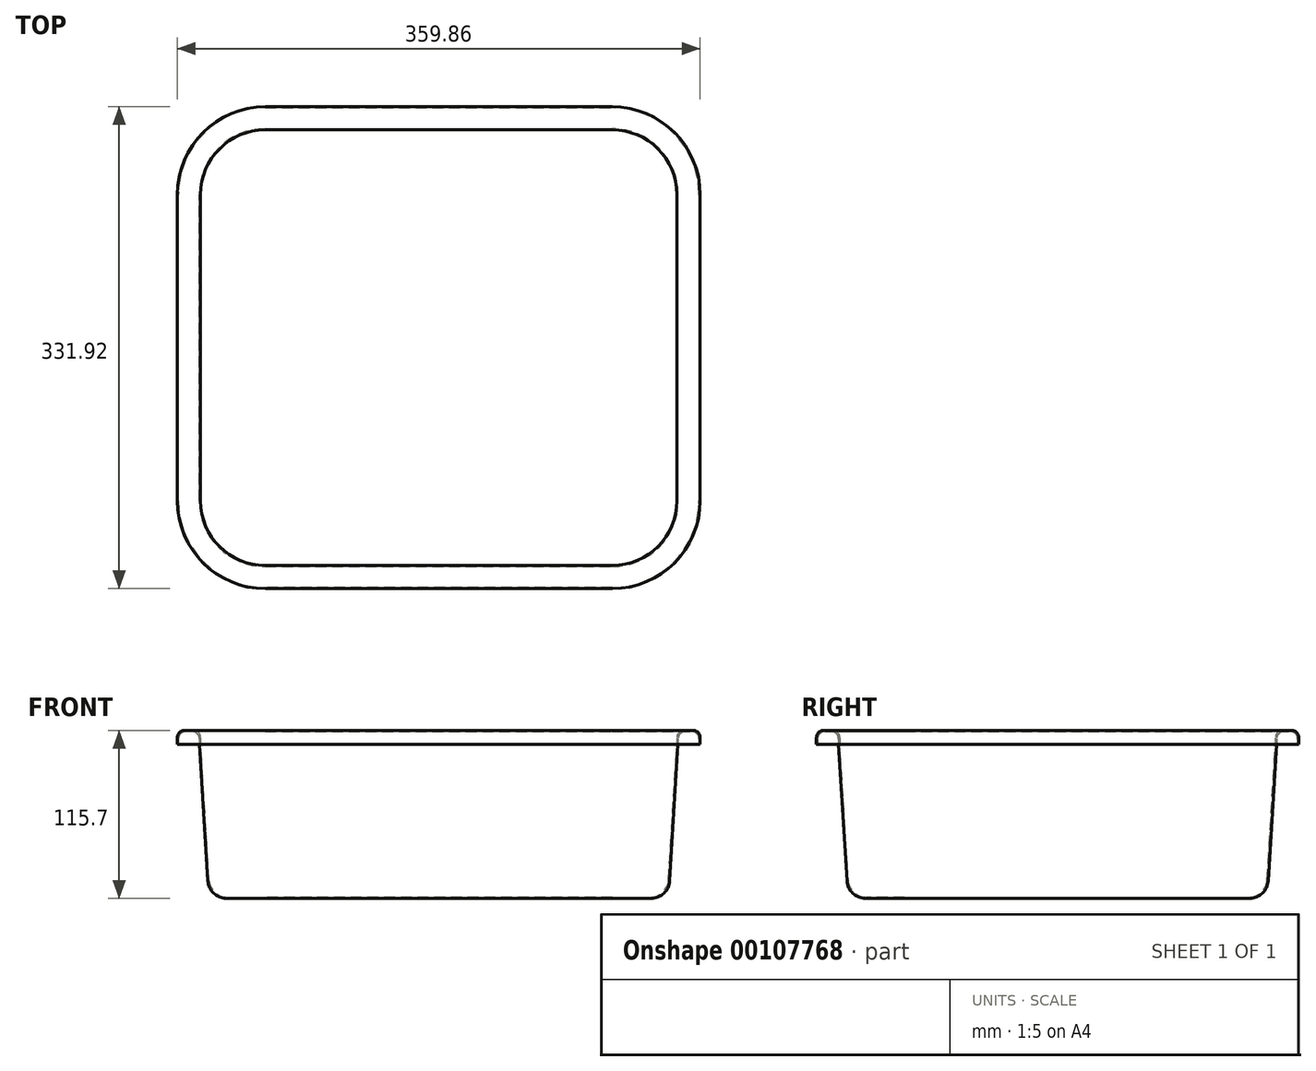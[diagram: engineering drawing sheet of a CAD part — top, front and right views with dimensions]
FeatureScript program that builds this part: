
annotation { "Feature Type Name" : "Feature", "Feature Type Description" : "" }
export const myFeature = defineFeature(function(context is Context, id is Id, definition is map)
    precondition{}
    {
        {
            var Q0;
            Q0=qCreatedBy(makeId("Top.planeOp"),FACE);
            var sketch = newSketch(context, id + "F0", { "sketchPlane" : qUnion([Q0])});
            skLineSegment(sketch, "E0.bottom", {"start": v(-119.38, -143.51) * mm, "end": v(119.38, -143.51) * mm});
            skLineSegment(sketch, "E0.top", {"start": v(-119.38, 143.51) * mm, "end": v(119.38, 143.51) * mm});
            skLineSegment(sketch, "E0.left", {"start": v(-157.48, -105.41) * mm, "end": v(-157.48, 105.41) * mm});
            skLineSegment(sketch, "E0.right", {"start": v(157.48, -105.41) * mm, "end": v(157.48, 105.41) * mm});
            skPoint(sketch, "E0.middle", {"position": v(0, 0) * mm});
            skPoint(sketch, "E1.visualSharp", {"position": v(-157.48, 143.51) * mm});
            skArc(sketch, "E1.filletArc", {"start": v(-119.38, 143.51) * mm, "mid": v(-146.32, 132.35) * mm, "end": v(-157.48, 105.41) * mm});
            skPoint(sketch, "E2.visualSharp", {"position": v(157.48, 143.51) * mm});
            skArc(sketch, "E2.filletArc", {"start": v(157.48, 105.41) * mm, "mid": v(146.32, 132.35) * mm, "end": v(119.38, 143.51) * mm});
            skPoint(sketch, "E3.visualSharp", {"position": v(157.48, -143.51) * mm});
            skArc(sketch, "E3.filletArc", {"start": v(119.38, -143.51) * mm, "mid": v(146.32, -132.35) * mm, "end": v(157.48, -105.41) * mm});
            skPoint(sketch, "E4.visualSharp", {"position": v(-157.48, -143.51) * mm});
            skArc(sketch, "E4.filletArc", {"start": v(-157.48, -105.41) * mm, "mid": v(-146.32, -132.35) * mm, "end": v(-119.38, -143.51) * mm});
            skSolve(sketch);
        }
        {
            var Q0;
            Q0 = qSketchRegion(id + "F0", true);
            extrude(context, id + "F1", {"entities" : qUnion([Q0]), "depth" : 105.4 * mm, "hasDraft" : true, "draftAngle" : 3.5 * degree});
        }
        {
            var Q0;
            Q0=makeQuery(id+"F1.opExtrude","CAP_FACE",FACE,{"disambiguationData":[OSD([sQuery(id+"F0.wireOp",EDGE,"E0.bottom"),sQuery(id+"F0.wireOp",EDGE,"E0.top"),sQuery(id+"F0.wireOp",EDGE,"E0.left"),sQuery(id+"F0.wireOp",EDGE,"E0.right")])],"isStart":false});
            shell(context, id + "F2", {"entities" : qUnion([Q0]), "thickness" : 0.76 * mm, "oppositeDirection" : true});
        }
        {
            var Q0;
            Q0=makeQuery(id+"F1.opExtrude","CAP_FACE",FACE,{"disambiguationData":[OSD([sQuery(id+"F0.wireOp",EDGE,"E0.bottom"),sQuery(id+"F0.wireOp",EDGE,"E0.top"),sQuery(id+"F0.wireOp",EDGE,"E0.left"),sQuery(id+"F0.wireOp",EDGE,"E0.right"),sQuery(id+"F0.wireOp",EDGE,"E1.filletArc"),sQuery(id+"F0.wireOp",EDGE,"E2.filletArc"),sQuery(id+"F0.wireOp",EDGE,"E3.filletArc"),sQuery(id+"F0.wireOp",EDGE,"E4.filletArc")])],"isStart":true});
            var Q1;
            Q1=makeQuery(id+"F2.opShell","OFFSET_FACE",FACE,{"disambiguationData":[OSD([sQuery(id+"F0.wireOp",EDGE,"E0.bottom"),sQuery(id+"F0.wireOp",EDGE,"E0.top"),sQuery(id+"F0.wireOp",EDGE,"E0.left"),sQuery(id+"F0.wireOp",EDGE,"E0.right"),sQuery(id+"F0.wireOp",EDGE,"E1.filletArc"),sQuery(id+"F0.wireOp",EDGE,"E2.filletArc"),sQuery(id+"F0.wireOp",EDGE,"E3.filletArc"),sQuery(id+"F0.wireOp",EDGE,"E4.filletArc")])]});
            fillet(context, id + "F3", {"entities" : qUnion([Q0, Q1]), "radius" : 12.7 * mm, "tangentPropagation" : true, "allowEdgeOverflow" : false});
        }
        {
            var Q0;
            Q0=makeQuery(id+"F1.opExtrude","CAP_FACE",FACE,{"disambiguationData":[OSD([sQuery(id+"F0.wireOp",EDGE,"E0.bottom"),sQuery(id+"F0.wireOp",EDGE,"E0.top"),sQuery(id+"F0.wireOp",EDGE,"E0.left"),sQuery(id+"F0.wireOp",EDGE,"E0.right"),sQuery(id+"F0.wireOp",EDGE,"E1.filletArc"),sQuery(id+"F0.wireOp",EDGE,"E2.filletArc"),sQuery(id+"F0.wireOp",EDGE,"E3.filletArc"),sQuery(id+"F0.wireOp",EDGE,"E4.filletArc")])],"isStart":false});
            var sketch = newSketch(context, id + "F4", { "sketchPlane" : qUnion([Q0])});
            skLineSegment(sketch, "E5.0", {"start": v(-119.38, 165.96) * mm, "end": v(119.38, 165.96) * mm});
            skArc(sketch, "E5.1", {"start": v(179.93, 105.41) * mm, "mid": v(162.2, 148.23) * mm, "end": v(119.38, 165.96) * mm});
            skArc(sketch, "E5.2", {"start": v(-119.38, 165.96) * mm, "mid": v(-162.2, 148.23) * mm, "end": v(-179.93, 105.41) * mm});
            skLineSegment(sketch, "E5.3", {"start": v(179.93, -105.41) * mm, "end": v(179.93, 105.41) * mm});
            skLineSegment(sketch, "E5.4", {"start": v(-179.93, -105.41) * mm, "end": v(-179.93, 105.41) * mm});
            skArc(sketch, "E5.5", {"start": v(-179.93, -105.41) * mm, "mid": v(-162.2, -148.23) * mm, "end": v(-119.38, -165.96) * mm});
            skLineSegment(sketch, "E5.6", {"start": v(-119.38, -165.96) * mm, "end": v(119.38, -165.96) * mm});
            skArc(sketch, "E5.7", {"start": v(119.38, -165.96) * mm, "mid": v(162.2, -148.23) * mm, "end": v(179.93, -105.41) * mm});
            skLineSegment(sketch, "E6.0", {"start": v(-119.38, -149.96) * mm, "end": v(119.38, -149.96) * mm});
            skArc(sketch, "E6.1", {"start": v(-163.93, -105.41) * mm, "mid": v(-150.88, -136.9) * mm, "end": v(-119.38, -149.96) * mm});
            skLineSegment(sketch, "E6.2", {"start": v(-163.93, -105.41) * mm, "end": v(-163.93, 105.41) * mm});
            skArc(sketch, "E6.3", {"start": v(-119.38, 149.96) * mm, "mid": v(-150.88, 136.9) * mm, "end": v(-163.93, 105.41) * mm});
            skLineSegment(sketch, "E6.4", {"start": v(-119.38, 149.96) * mm, "end": v(119.38, 149.96) * mm});
            skArc(sketch, "E6.5", {"start": v(163.93, 105.41) * mm, "mid": v(150.88, 136.9) * mm, "end": v(119.38, 149.96) * mm});
            skLineSegment(sketch, "E6.6", {"start": v(163.93, -105.41) * mm, "end": v(163.93, 105.41) * mm});
            skArc(sketch, "E6.7", {"start": v(119.38, -149.96) * mm, "mid": v(150.88, -136.9) * mm, "end": v(163.93, -105.41) * mm});
            skSolve(sketch);
        }
        {
            var Q0;
            Q0 = qSketchRegion(id + "F4", true);
            extrude(context, id + "F5", {"entities" : qUnion([Q0]), "operationType" : NewBodyOperationType.ADD, "depth" : 9.52 * mm});
        }
        {
            var Q0;
            Q0=makeQuery(id+"F5.opExtrude","CAP_FACE",FACE,{"disambiguationData":[OSD([sQuery(id+"F4.wireOp",EDGE,"E5.0"),sQuery(id+"F4.wireOp",EDGE,"E5.1"),sQuery(id+"F4.wireOp",EDGE,"E5.2"),sQuery(id+"F4.wireOp",EDGE,"E5.3"),sQuery(id+"F4.wireOp",EDGE,"E5.4"),sQuery(id+"F4.wireOp",EDGE,"E5.5"),sQuery(id+"F4.wireOp",EDGE,"E5.6"),sQuery(id+"F4.wireOp",EDGE,"E5.7"),sQuery(id+"F4.wireOp",EDGE,"E6.0"),sQuery(id+"F4.wireOp",EDGE,"E6.1"),sQuery(id+"F4.wireOp",EDGE,"E6.2"),sQuery(id+"F4.wireOp",EDGE,"E6.3"),sQuery(id+"F4.wireOp",EDGE,"E6.4"),sQuery(id+"F4.wireOp",EDGE,"E6.5"),sQuery(id+"F4.wireOp",EDGE,"E6.6"),sQuery(id+"F4.wireOp",EDGE,"E6.7")])],"isStart":true});
            var sketch = newSketch(context, id + "F6", { "sketchPlane" : qUnion([Q0])});
            skArc(sketch, "E7.0", {"start": v(-179.17, -105.41) * mm, "mid": v(-161.66, -147.69) * mm, "end": v(-119.38, -165.2) * mm});
            skLineSegment(sketch, "E7.1", {"start": v(-179.17, 105.41) * mm, "end": v(-179.17, -105.41) * mm});
            skLineSegment(sketch, "E7.2", {"start": v(-119.38, -165.2) * mm, "end": v(119.38, -165.2) * mm});
            skArc(sketch, "E7.3", {"start": v(-119.38, 165.2) * mm, "mid": v(-161.66, 147.69) * mm, "end": v(-179.17, 105.41) * mm});
            skArc(sketch, "E7.4", {"start": v(119.38, -165.2) * mm, "mid": v(161.66, -147.69) * mm, "end": v(179.17, -105.41) * mm});
            skLineSegment(sketch, "E7.5", {"start": v(179.17, -105.41) * mm, "end": v(179.17, 105.41) * mm});
            skArc(sketch, "E7.6", {"start": v(179.17, 105.41) * mm, "mid": v(161.66, 147.69) * mm, "end": v(119.38, 165.2) * mm});
            skLineSegment(sketch, "E7.7", {"start": v(119.38, 165.2) * mm, "end": v(-119.38, 165.2) * mm});
            skSolve(sketch);
        }
        {
            var Q0;
            Q0=makeQuery(id+"F6.imprint","IMPRINT",FACE,{"disambiguationData":[TD([[makeQuery(id+"F6.imprint","IMPRINT",EDGE,{"derivedFrom":sQuery(id+"F6.wireOp",EDGE,"E7.0")}),1.0]])]});
            extrude(context, id + "F7", {"entities" : qUnion([Q0]), "operationType" : NewBodyOperationType.REMOVE, "oppositeDirection" : true, "depth" : 8.76 * mm});
        }
        {
            var Q0;
            Q0=makeQuery(id+"F7.boolean.opBoolean","COPY",FACE,{"derivedFrom":makeQuery(id+"F7.opExtrude","CAP_FACE",FACE,{"disambiguationData":[OSD([sQuery(id+"F0.wireOp",EDGE,"E0.bottom"),sQuery(id+"F0.wireOp",EDGE,"E0.top"),sQuery(id+"F0.wireOp",EDGE,"E0.left"),sQuery(id+"F0.wireOp",EDGE,"E0.right"),sQuery(id+"F0.wireOp",EDGE,"E1.filletArc"),sQuery(id+"F0.wireOp",EDGE,"E2.filletArc"),sQuery(id+"F0.wireOp",EDGE,"E3.filletArc"),sQuery(id+"F0.wireOp",EDGE,"E4.filletArc"),sQuery(id+"F6.wireOp",EDGE,"E7.0"),sQuery(id+"F6.wireOp",EDGE,"E7.1"),sQuery(id+"F6.wireOp",EDGE,"E7.2"),sQuery(id+"F6.wireOp",EDGE,"E7.3"),sQuery(id+"F6.wireOp",EDGE,"E7.4"),sQuery(id+"F6.wireOp",EDGE,"E7.5"),sQuery(id+"F6.wireOp",EDGE,"E7.6"),sQuery(id+"F6.wireOp",EDGE,"E7.7")])],"isStart":false})});
            var Q1;
            Q1=makeQuery(id+"F5.opExtrude","CAP_FACE",FACE,{"disambiguationData":[OSD([sQuery(id+"F4.wireOp",EDGE,"E5.0"),sQuery(id+"F4.wireOp",EDGE,"E5.1"),sQuery(id+"F4.wireOp",EDGE,"E5.2"),sQuery(id+"F4.wireOp",EDGE,"E5.3"),sQuery(id+"F4.wireOp",EDGE,"E5.4"),sQuery(id+"F4.wireOp",EDGE,"E5.5"),sQuery(id+"F4.wireOp",EDGE,"E5.6"),sQuery(id+"F4.wireOp",EDGE,"E5.7"),sQuery(id+"F4.wireOp",EDGE,"E6.0"),sQuery(id+"F4.wireOp",EDGE,"E6.1"),sQuery(id+"F4.wireOp",EDGE,"E6.2"),sQuery(id+"F4.wireOp",EDGE,"E6.3"),sQuery(id+"F4.wireOp",EDGE,"E6.4"),sQuery(id+"F4.wireOp",EDGE,"E6.5"),sQuery(id+"F4.wireOp",EDGE,"E6.6"),sQuery(id+"F4.wireOp",EDGE,"E6.7")])],"isStart":false});
            fillet(context, id + "F8", {"entities" : qUnion([Q0, Q1]), "radius" : 5.08 * mm, "tangentPropagation" : true, "allowEdgeOverflow" : false});
        }
    });
